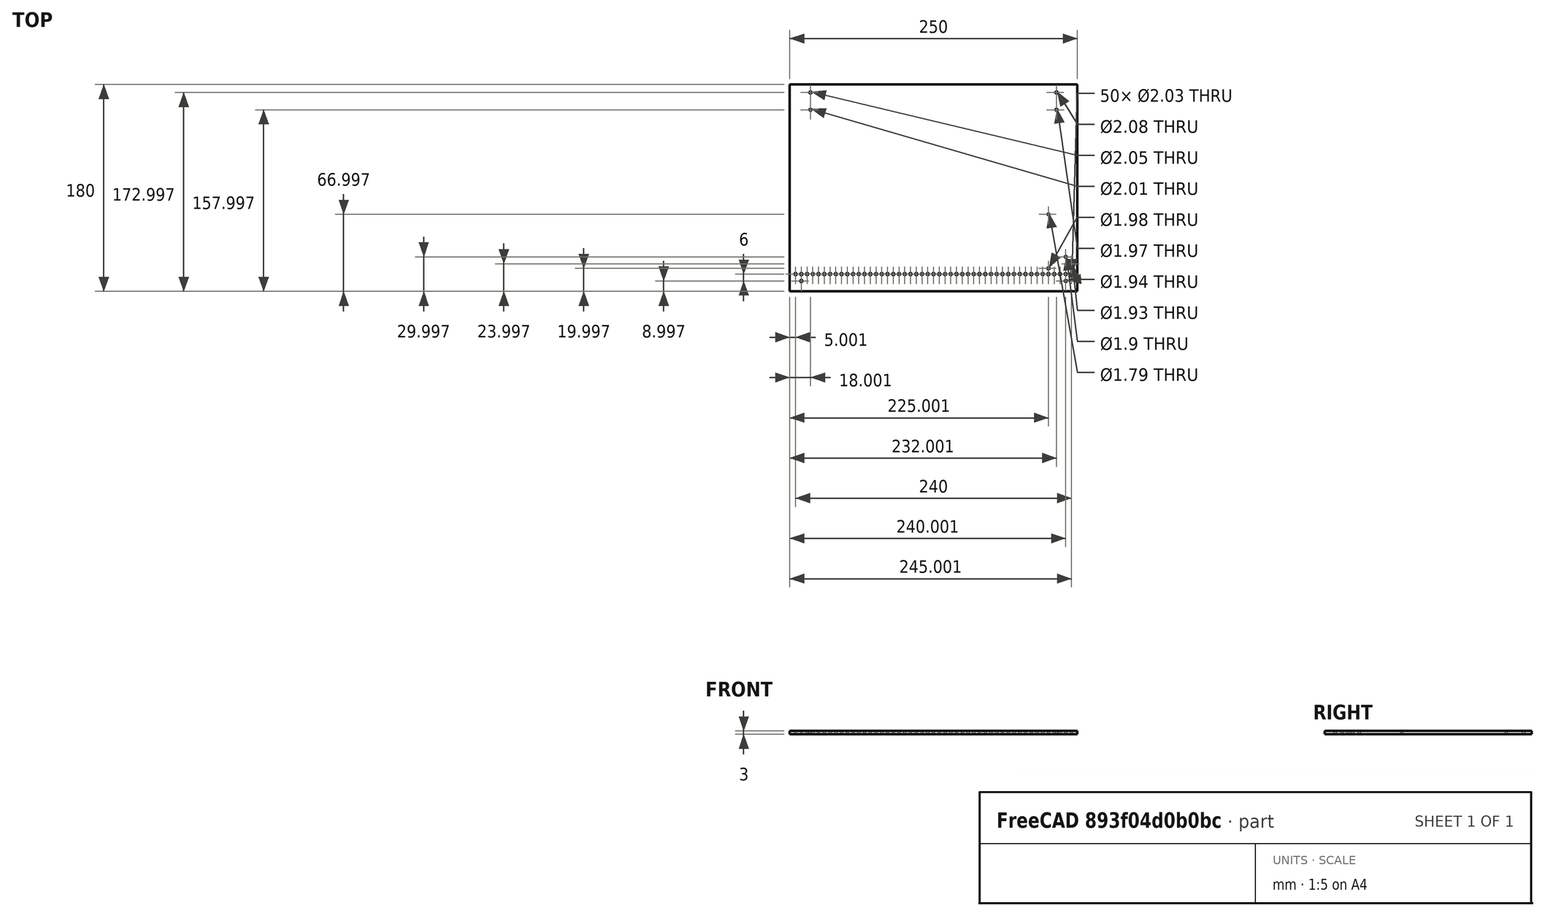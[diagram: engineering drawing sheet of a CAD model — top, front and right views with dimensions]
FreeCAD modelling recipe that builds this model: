
FCSTD DOCUMENT  (FreeCAD 0.19R24267 +148 (Git))
Label: SideWall
License: All rights reserved
LicenseURL: http://en.wikipedia.org/wiki/All_rights_reserved
objects: Sketcher::SketchObject×1, PartDesign::Pad×1, PartDesign::Body×1
note: 4 computed .brp shape members not serialized (recipe doc carries the construction recipe); baked Part::Feature solids carry a one-line shape summary decoded from their .brp

FEATURE [Sketcher::SketchObject] Sketch  label="Side"
  FullyConstrained = false
  MapMode = 5
  Support = -> [XY_Plane]
  sketch-geometry (75):
    g0: LineSegment StartX=-319.259 StartY=-46.8432 StartZ=0 EndX=-69.2592 EndY=-46.8432 EndZ=0
    g1: LineSegment StartX=-69.2592 StartY=-46.8432 StartZ=0 EndX=-69.2592 EndY=-226.843 EndZ=0
    g2: LineSegment StartX=-69.2592 StartY=-226.843 StartZ=0 EndX=-319.259 EndY=-226.843 EndZ=0
    g3: LineSegment StartX=-319.259 StartY=-226.843 StartZ=0 EndX=-319.259 EndY=-46.8432 EndZ=0
    g4: GeomPoint X=-301.259 Y=-53.8432 Z=0
    g5: GeomPoint X=-301.259 Y=-68.8432 Z=0
    g6: GeomPoint X=0 Y=0 Z=0
    g7: GeomPoint X=-87.2592 Y=-53.8432 Z=0
    g8: GeomPoint X=-87.2592 Y=-68.8432 Z=0
    g9: GeomPoint X=-309.259 Y=-217.843 Z=0
    g10: GeomPoint X=-79.2592 Y=-217.843 Z=0
    g11: GeomPoint X=-94.2592 Y=-159.843 Z=0
    g12: GeomPoint X=-94.2592 Y=-206.843 Z=0
    g13: Circle CenterX=-301.259 CenterY=-53.8432 CenterZ=0 NormalX=0 NormalY=0 NormalZ=1 AngleXU=0 Radius=1.02399
    g14: Circle CenterX=-301.259 CenterY=-68.8432 CenterZ=0 NormalX=0 NormalY=0 NormalZ=1 AngleXU=0 Radius=1.00473
    g15: Circle CenterX=-87.2592 CenterY=-53.8432 CenterZ=0 NormalX=0 NormalY=0 NormalZ=1 AngleXU=0 Radius=1.04059
    g16: Circle CenterX=-87.2592 CenterY=-68.8432 CenterZ=0 NormalX=0 NormalY=0 NormalZ=1 AngleXU=0 Radius=0.983061
    g17: Circle CenterX=-94.2592 CenterY=-159.843 CenterZ=0 NormalX=0 NormalY=0 NormalZ=1 AngleXU=0 Radius=0.893442
    g18: Circle CenterX=-94.2592 CenterY=-206.843 CenterZ=0 NormalX=0 NormalY=0 NormalZ=1 AngleXU=0 Radius=0.989754
    g19: Circle CenterX=-79.2592 CenterY=-217.843 CenterZ=0 NormalX=0 NormalY=0 NormalZ=1 AngleXU=0 Radius=0.971299
    g20: Circle CenterX=-309.259 CenterY=-217.843 CenterZ=0 NormalX=0 NormalY=0 NormalZ=1 AngleXU=0 Radius=1.01609
    g21: GeomPoint X=-74.2592 Y=-211.843 Z=0
    g22: Circle CenterX=-74.2592 CenterY=-211.843 CenterZ=0 NormalX=0 NormalY=0 NormalZ=1 AngleXU=0 Radius=1.01284
    g23: Circle CenterX=-79.2592 CenterY=-211.843 CenterZ=0 NormalX=0 NormalY=0 NormalZ=1 AngleXU=0 Radius=1.01284
    g24: Circle CenterX=-84.2592 CenterY=-211.843 CenterZ=0 NormalX=0 NormalY=0 NormalZ=1 AngleXU=0 Radius=1.01284
    g25: Circle CenterX=-89.2592 CenterY=-211.843 CenterZ=0 NormalX=0 NormalY=0 NormalZ=1 AngleXU=0 Radius=1.01284
    g26: Circle CenterX=-94.2592 CenterY=-211.843 CenterZ=0 NormalX=0 NormalY=0 NormalZ=1 AngleXU=0 Radius=1.01284
    g27: Circle CenterX=-99.2592 CenterY=-211.843 CenterZ=0 NormalX=0 NormalY=0 NormalZ=1 AngleXU=0 Radius=1.01284
    g28: Circle CenterX=-104.259 CenterY=-211.843 CenterZ=0 NormalX=0 NormalY=0 NormalZ=1 AngleXU=0 Radius=1.01284
    g29: Circle CenterX=-109.259 CenterY=-211.843 CenterZ=0 NormalX=0 NormalY=0 NormalZ=1 AngleXU=0 Radius=1.01284
    g30: Circle CenterX=-114.259 CenterY=-211.843 CenterZ=0 NormalX=0 NormalY=0 NormalZ=1 AngleXU=0 Radius=1.01284
    g31: Circle CenterX=-119.259 CenterY=-211.843 CenterZ=0 NormalX=0 NormalY=0 NormalZ=1 AngleXU=0 Radius=1.01284
    g32: Circle CenterX=-124.259 CenterY=-211.843 CenterZ=0 NormalX=0 NormalY=0 NormalZ=1 AngleXU=0 Radius=1.01284
    g33: Circle CenterX=-129.259 CenterY=-211.843 CenterZ=0 NormalX=0 NormalY=0 NormalZ=1 AngleXU=0 Radius=1.01284
    g34: Circle CenterX=-134.259 CenterY=-211.843 CenterZ=0 NormalX=0 NormalY=0 NormalZ=1 AngleXU=0 Radius=1.01284
    g35: Circle CenterX=-139.259 CenterY=-211.843 CenterZ=0 NormalX=0 NormalY=0 NormalZ=1 AngleXU=0 Radius=1.01284
    g36: Circle CenterX=-144.259 CenterY=-211.843 CenterZ=0 NormalX=0 NormalY=0 NormalZ=1 AngleXU=0 Radius=1.01284
    g37: Circle CenterX=-149.259 CenterY=-211.843 CenterZ=0 NormalX=0 NormalY=0 NormalZ=1 AngleXU=0 Radius=1.01284
    g38: Circle CenterX=-154.259 CenterY=-211.843 CenterZ=0 NormalX=0 NormalY=0 NormalZ=1 AngleXU=0 Radius=1.01284
    g39: Circle CenterX=-159.259 CenterY=-211.843 CenterZ=0 NormalX=0 NormalY=0 NormalZ=1 AngleXU=0 Radius=1.01284
    g40: Circle CenterX=-164.259 CenterY=-211.843 CenterZ=0 NormalX=0 NormalY=0 NormalZ=1 AngleXU=0 Radius=1.01284
    g41: Circle CenterX=-169.259 CenterY=-211.843 CenterZ=0 NormalX=0 NormalY=0 NormalZ=1 AngleXU=0 Radius=1.01284
    g42: Circle CenterX=-174.259 CenterY=-211.843 CenterZ=0 NormalX=0 NormalY=0 NormalZ=1 AngleXU=0 Radius=1.01284
    g43: Circle CenterX=-179.259 CenterY=-211.843 CenterZ=0 NormalX=0 NormalY=0 NormalZ=1 AngleXU=0 Radius=1.01284
    g44: Circle CenterX=-184.259 CenterY=-211.843 CenterZ=0 NormalX=0 NormalY=0 NormalZ=1 AngleXU=0 Radius=1.01284
    g45: Circle CenterX=-189.259 CenterY=-211.843 CenterZ=0 NormalX=0 NormalY=0 NormalZ=1 AngleXU=0 Radius=1.01284
    g46: Circle CenterX=-194.259 CenterY=-211.843 CenterZ=0 NormalX=0 NormalY=0 NormalZ=1 AngleXU=0 Radius=1.01284
    g47: Circle CenterX=-199.259 CenterY=-211.843 CenterZ=0 NormalX=0 NormalY=0 NormalZ=1 AngleXU=0 Radius=1.01284
    g48: Circle CenterX=-204.259 CenterY=-211.843 CenterZ=0 NormalX=0 NormalY=0 NormalZ=1 AngleXU=0 Radius=1.01284
    g49: Circle CenterX=-209.259 CenterY=-211.843 CenterZ=0 NormalX=0 NormalY=0 NormalZ=1 AngleXU=0 Radius=1.01284
    g50: Circle CenterX=-214.259 CenterY=-211.843 CenterZ=0 NormalX=0 NormalY=0 NormalZ=1 AngleXU=0 Radius=1.01284
    g51: Circle CenterX=-219.259 CenterY=-211.843 CenterZ=0 NormalX=0 NormalY=0 NormalZ=1 AngleXU=0 Radius=1.01284
    g52: Circle CenterX=-224.259 CenterY=-211.843 CenterZ=0 NormalX=0 NormalY=0 NormalZ=1 AngleXU=0 Radius=1.01284
    g53: Circle CenterX=-229.259 CenterY=-211.843 CenterZ=0 NormalX=0 NormalY=0 NormalZ=1 AngleXU=0 Radius=1.01284
    g54: Circle CenterX=-234.259 CenterY=-211.843 CenterZ=0 NormalX=0 NormalY=0 NormalZ=1 AngleXU=0 Radius=1.01284
    g55: Circle CenterX=-239.259 CenterY=-211.843 CenterZ=0 NormalX=0 NormalY=0 NormalZ=1 AngleXU=0 Radius=1.01284
    g56: Circle CenterX=-244.259 CenterY=-211.843 CenterZ=0 NormalX=0 NormalY=0 NormalZ=1 AngleXU=0 Radius=1.01284
    g57: Circle CenterX=-249.259 CenterY=-211.843 CenterZ=0 NormalX=0 NormalY=0 NormalZ=1 AngleXU=0 Radius=1.01284
    g58: Circle CenterX=-254.259 CenterY=-211.843 CenterZ=0 NormalX=0 NormalY=0 NormalZ=1 AngleXU=0 Radius=1.01284
    g59: Circle CenterX=-259.259 CenterY=-211.843 CenterZ=0 NormalX=0 NormalY=0 NormalZ=1 AngleXU=0 Radius=1.01284
    g60: Circle CenterX=-264.259 CenterY=-211.843 CenterZ=0 NormalX=0 NormalY=0 NormalZ=1 AngleXU=0 Radius=1.01284
    g61: Circle CenterX=-269.259 CenterY=-211.843 CenterZ=0 NormalX=0 NormalY=0 NormalZ=1 AngleXU=0 Radius=1.01284
    g62: Circle CenterX=-274.259 CenterY=-211.843 CenterZ=0 NormalX=0 NormalY=0 NormalZ=1 AngleXU=0 Radius=1.01284
    g63: Circle CenterX=-279.259 CenterY=-211.843 CenterZ=0 NormalX=0 NormalY=0 NormalZ=1 AngleXU=0 Radius=1.01284
    g64: Circle CenterX=-284.259 CenterY=-211.843 CenterZ=0 NormalX=0 NormalY=0 NormalZ=1 AngleXU=0 Radius=1.01284
    g65: Circle CenterX=-289.259 CenterY=-211.843 CenterZ=0 NormalX=0 NormalY=0 NormalZ=1 AngleXU=0 Radius=1.01284
    g66: Circle CenterX=-294.259 CenterY=-211.843 CenterZ=0 NormalX=0 NormalY=0 NormalZ=1 AngleXU=0 Radius=1.01284
    g67: Circle CenterX=-299.259 CenterY=-211.843 CenterZ=0 NormalX=0 NormalY=0 NormalZ=1 AngleXU=0 Radius=1.01284
    g68: Circle CenterX=-304.259 CenterY=-211.843 CenterZ=0 NormalX=0 NormalY=0 NormalZ=1 AngleXU=0 Radius=1.01284
    g69: Circle CenterX=-309.259 CenterY=-211.843 CenterZ=0 NormalX=0 NormalY=0 NormalZ=1 AngleXU=0 Radius=1.01284
    g70: Circle CenterX=-314.259 CenterY=-211.843 CenterZ=0 NormalX=0 NormalY=0 NormalZ=1 AngleXU=0 Radius=1.01284
    g71: GeomPoint X=-74.2592 Y=-202.843 Z=0
    g72: GeomPoint X=-79.2592 Y=-196.843 Z=0
    g73: Circle CenterX=-74.2592 CenterY=-202.843 CenterZ=0 NormalX=0 NormalY=0 NormalZ=1 AngleXU=0 Radius=0.965648
    g74: Circle CenterX=-79.2592 CenterY=-196.843 CenterZ=0 NormalX=0 NormalY=0 NormalZ=1 AngleXU=0 Radius=0.950368
  constraints (39):
    c: Coincident(g0,g1)
    c: Coincident(g1,g2)
    c: Coincident(g2,g3)
    c: Coincident(g3,g0)
    c: Horizontal(g0)
    c: Horizontal(g2)
    c: Vertical(g1)
    c: Vertical(g3)
    c: Distance(g0,g2) = 180
    c: Distance(g0) = 250
    c: Distance(g4,g5) = 15
    c: Distance(g4,g0) = 7
    c: Distance(g4,g3) = 18
    c: Distance(g8,g7) = 15
    c: Distance(g7,g0) = 7
    c: Distance(g7,g1) = 18
    c: Distance(g9,g2) = 9
    c: Distance(g9,g3) = 10
    c: Distance(g10,g2) = 9
    c: Distance(g10,g1) = 10
    c: Distance(g12,g2) = 20
    c: Distance(g12,g11) = 47
    c: Distance(g11,g1) = 25
    c: Coincident(g13,g4)
    c: Coincident(g14,g5)
    c: Coincident(g15,g7)
    c: Coincident(g16,g8)
    c: Coincident(g17,g11)
    c: Coincident(g18,g12)
    c: Coincident(g19,g10)
    c: Coincident(g20,g9)
    c: Distance(g21,g1) = 5
    c: Distance(g21,g2) = 15
    c: Coincident(g22,g21)
    c: Distance(g71,g22) = 9
    c: Distance(g72,g23) = 15
    c: Coincident(g73,g71)
    c: Coincident(g74,g72)
    c: Distance(g37,g36) = 5
FEATURE [PartDesign::Pad] Pad
  Direction = (1,1,1)
  Length = 3
  Length2 = 100
  Profile = -> Sketch
  Type = 0
FEATURE [PartDesign::Body] Body
  Group = -> [Sketch,Pad]
  Origin = -> Origin
  Tip = -> Pad
